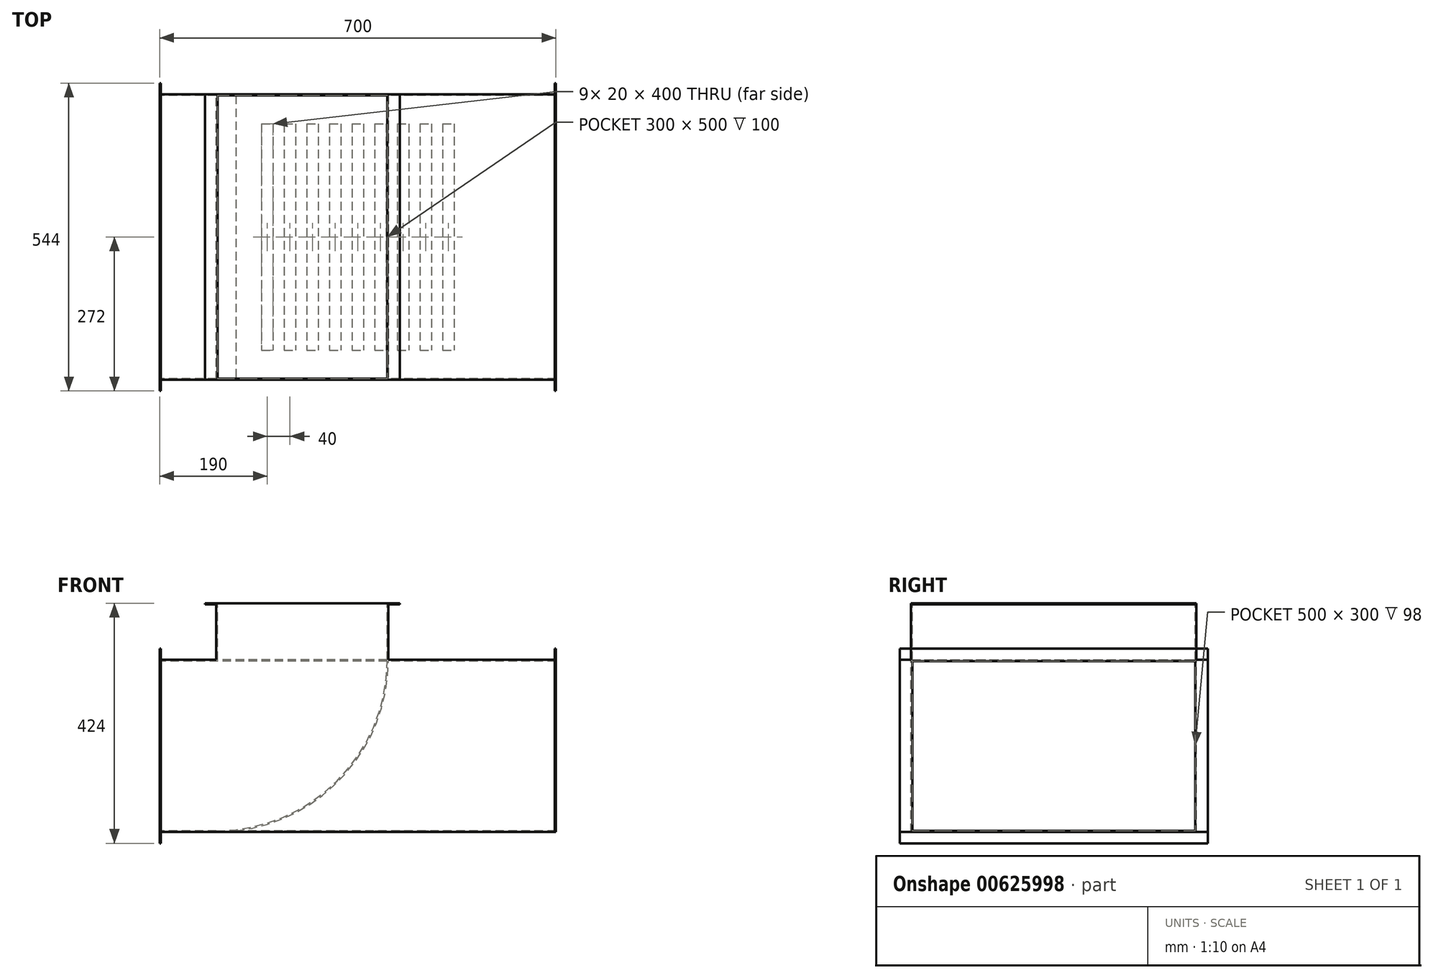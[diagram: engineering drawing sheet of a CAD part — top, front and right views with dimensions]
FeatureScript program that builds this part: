
annotation { "Feature Type Name" : "Feature", "Feature Type Description" : "" }
export const myFeature = defineFeature(function(context is Context, id is Id, definition is map)
    precondition{}
    {
        {
            var Q0;
            Q0=qCreatedBy(makeId("Right.planeOp"),FACE);
            var sketch = newSketch(context, id + "F0", { "sketchPlane" : qUnion([Q0])});
            skLineSegment(sketch, "E0.bottom", {"start": v(0, 0) * mm, "end": v(504, 0) * mm});
            skLineSegment(sketch, "E0.top", {"start": v(0, 304) * mm, "end": v(504, 304) * mm});
            skLineSegment(sketch, "E0.left", {"start": v(0, 0) * mm, "end": v(0, 304) * mm});
            skLineSegment(sketch, "E0.right", {"start": v(504, 0) * mm, "end": v(504, 304) * mm});
            skLineSegment(sketch, "E1.top", {"start": v(0, 324) * mm, "end": v(504, 324) * mm});
            skLineSegment(sketch, "E1.left", {"start": v(0, 304) * mm, "end": v(0, 324) * mm});
            skLineSegment(sketch, "E1.right", {"start": v(504, 304) * mm, "end": v(504, 324) * mm});
            skLineSegment(sketch, "E2.bottom", {"start": v(0, 304) * mm, "end": v(-20, 304) * mm});
            skLineSegment(sketch, "E2.top", {"start": v(0, 0) * mm, "end": v(-20, 0) * mm});
            skLineSegment(sketch, "E2.left", {"start": v(0, 304) * mm, "end": v(0, 0) * mm});
            skLineSegment(sketch, "E2.right", {"start": v(-20, 304) * mm, "end": v(-20, 0) * mm});
            skLineSegment(sketch, "E3.bottom", {"start": v(504, 304) * mm, "end": v(524, 304) * mm});
            skLineSegment(sketch, "E3.top", {"start": v(504, 0) * mm, "end": v(524, 0) * mm});
            skLineSegment(sketch, "E3.left", {"start": v(504, 304) * mm, "end": v(504, 0) * mm});
            skLineSegment(sketch, "E3.right", {"start": v(524, 304) * mm, "end": v(524, 0) * mm});
            skLineSegment(sketch, "E4.bottom", {"start": v(504, 0) * mm, "end": v(0, 0) * mm});
            skLineSegment(sketch, "E4.top", {"start": v(504, -20) * mm, "end": v(0, -20) * mm});
            skLineSegment(sketch, "E4.left", {"start": v(504, 0) * mm, "end": v(504, -20) * mm});
            skLineSegment(sketch, "E4.right", {"start": v(0, 0) * mm, "end": v(0, -20) * mm});
            skLineSegment(sketch, "E5.bottom", {"start": v(2, 2) * mm, "end": v(502, 2) * mm});
            skLineSegment(sketch, "E5.top", {"start": v(2, 302) * mm, "end": v(502, 302) * mm});
            skLineSegment(sketch, "E5.left", {"start": v(2, 2) * mm, "end": v(2, 302) * mm});
            skLineSegment(sketch, "E5.right", {"start": v(502, 2) * mm, "end": v(502, 302) * mm});
            skSolve(sketch);
        }
        {
            var Q0;
            Q0=makeQuery(id+"F0.imprint","IMPRINT",FACE,{"disambiguationData":[TD([[makeQuery(id+"F0.imprint","IMPRINT",EDGE,{"derivedFrom":sQuery(id+"F0.wireOp",EDGE,"E0.top")}),-1.0]])]});
            extrude(context, id + "F1", {"entities" : qUnion([Q0]), "depth" : 700 * mm, "offsetDistance" : 25 * mm});
        }
        {
            var Q0;
            Q0=makeQuery(id+"F0.imprint","IMPRINT",FACE,{"disambiguationData":[TD([[makeQuery(id+"F0.imprint","IMPRINT",EDGE,{"derivedFrom":sQuery(id+"F0.wireOp",EDGE,"E0.top")}),1.0]])]});
            var Q1;
            Q1=makeQuery(id+"F0.imprint","IMPRINT",FACE,{"disambiguationData":[TD([[makeQuery(id+"F0.imprint","IMPRINT",EDGE,{"derivedFrom":sQuery(id+"F0.wireOp",EDGE,"E2.bottom")}),1.0]])]});
            var Q2;
            Q2=makeQuery(id+"F0.imprint","IMPRINT",FACE,{"disambiguationData":[TD([[makeQuery(id+"F0.imprint","IMPRINT",EDGE,{"derivedFrom":sQuery(id+"F0.wireOp",EDGE,"E4.bottom")}),1.0]])]});
            var Q3;
            Q3=makeQuery(id+"F0.imprint","IMPRINT",FACE,{"disambiguationData":[TD([[makeQuery(id+"F0.imprint","IMPRINT",EDGE,{"derivedFrom":sQuery(id+"F0.wireOp",EDGE,"E3.bottom")}),-1.0]])]});
            extrude(context, id + "F2", {"entities" : qUnion([Q0, Q1, Q2, Q3]), "operationType" : NewBodyOperationType.ADD, "depth" : 700 * mm, "offsetDistance" : 25 * mm});
        }
        {
            var Q0;
            Q0=makeQuery(id+"F0.imprint","IMPRINT",FACE,{"disambiguationData":[TD([[makeQuery(id+"F0.imprint","IMPRINT",EDGE,{"derivedFrom":sQuery(id+"F0.wireOp",EDGE,"E0.top")}),1.0]])]});
            var Q1;
            Q1=makeQuery(id+"F0.imprint","IMPRINT",FACE,{"disambiguationData":[TD([[makeQuery(id+"F0.imprint","IMPRINT",EDGE,{"derivedFrom":sQuery(id+"F0.wireOp",EDGE,"E3.bottom")}),-1.0]])]});
            var Q2;
            Q2=makeQuery(id+"F0.imprint","IMPRINT",FACE,{"disambiguationData":[TD([[makeQuery(id+"F0.imprint","IMPRINT",EDGE,{"derivedFrom":sQuery(id+"F0.wireOp",EDGE,"E4.bottom")}),1.0]])]});
            var Q3;
            Q3=makeQuery(id+"F0.imprint","IMPRINT",FACE,{"disambiguationData":[TD([[makeQuery(id+"F0.imprint","IMPRINT",EDGE,{"derivedFrom":sQuery(id+"F0.wireOp",EDGE,"E2.bottom")}),1.0]])]});
            extrude(context, id + "F3", {"entities" : qUnion([Q0, Q1, Q2, Q3]), "operationType" : NewBodyOperationType.REMOVE, "depth" : 698 * mm, "offsetDistance" : 25 * mm});
        }
        {
            var Q0;
            Q0=makeQuery(id+"F0.imprint","IMPRINT",FACE,{"disambiguationData":[TD([[makeQuery(id+"F0.imprint","IMPRINT",EDGE,{"derivedFrom":sQuery(id+"F0.wireOp",EDGE,"E0.top")}),1.0]])]});
            var Q1;
            Q1=makeQuery(id+"F0.imprint","IMPRINT",FACE,{"disambiguationData":[TD([[makeQuery(id+"F0.imprint","IMPRINT",EDGE,{"derivedFrom":sQuery(id+"F0.wireOp",EDGE,"E3.bottom")}),-1.0]])]});
            var Q2;
            Q2=makeQuery(id+"F0.imprint","IMPRINT",FACE,{"disambiguationData":[TD([[makeQuery(id+"F0.imprint","IMPRINT",EDGE,{"derivedFrom":sQuery(id+"F0.wireOp",EDGE,"E4.bottom")}),1.0]])]});
            var Q3;
            Q3=makeQuery(id+"F0.imprint","IMPRINT",FACE,{"disambiguationData":[TD([[makeQuery(id+"F0.imprint","IMPRINT",EDGE,{"derivedFrom":sQuery(id+"F0.wireOp",EDGE,"E2.bottom")}),1.0]])]});
            extrude(context, id + "F4", {"entities" : qUnion([Q0, Q1, Q2, Q3]), "operationType" : NewBodyOperationType.ADD, "depth" : 2 * mm, "offsetDistance" : 25 * mm});
        }
        {
            var Q0;
            Q0=makeQuery(id+"F1.opExtrude","CAP_VERTEX",VERTEX,{"disambiguationData":[OSD([sQuery(id+"F0.wireOp",EDGE,"E5.top"),sQuery(id+"F0.wireOp",EDGE,"E5.left")])],"isStart":false});
            var Q1;
            Q1=makeQuery(id+"F1.opExtrude","CAP_VERTEX",VERTEX,{"disambiguationData":[OSD([sQuery(id+"F0.wireOp",EDGE,"E5.top"),sQuery(id+"F0.wireOp",EDGE,"E5.right")])],"isStart":false});
            var Q2;
            Q2=makeQuery(id+"F1.opExtrude","CAP_VERTEX",VERTEX,{"disambiguationData":[OSD([sQuery(id+"F0.wireOp",EDGE,"E5.bottom"),sQuery(id+"F0.wireOp",EDGE,"E5.right")])],"isStart":false});
            cPlane(context, id + "F5", {"entities" : qUnion([Q0, Q1, Q2]), "cplaneType" : CPlaneType.THREE_POINT, "offset" : 25 * mm, "width" : 150 * mm, "height" : 150 * mm});
        }
        {
            var Q0;
            Q0=qCreatedBy(id+"F5.planeOp",FACE);
            var sketch = newSketch(context, id + "F6", { "sketchPlane" : qUnion([Q0])});
            skLineSegment(sketch, "E6.0", {"start": v(2, 2) * mm, "end": v(2, 302) * mm});
            skLineSegment(sketch, "E7.0", {"start": v(2, 302) * mm, "end": v(502, 302) * mm});
            skLineSegment(sketch, "E8.0", {"start": v(502, 2) * mm, "end": v(502, 302) * mm});
            skLineSegment(sketch, "E9.0", {"start": v(2, 2) * mm, "end": v(502, 2) * mm});
            skSolve(sketch);
        }
        {
            var Q0;
            Q0=makeQuery(id+"F1.opExtrude","SWEPT_BODY",BODY,{"disambiguationData":[OSD([sQuery(id+"F0.wireOp",EDGE,"E0.top"),sQuery(id+"F0.wireOp",EDGE,"E2.left"),sQuery(id+"F0.wireOp",EDGE,"E3.left"),sQuery(id+"F0.wireOp",EDGE,"E4.bottom"),sQuery(id+"F0.wireOp",EDGE,"E5.bottom"),sQuery(id+"F0.wireOp",EDGE,"E5.top"),sQuery(id+"F0.wireOp",EDGE,"E5.left"),sQuery(id+"F0.wireOp",EDGE,"E5.right")])]});
            transform(context, id + "F7", {"entities" : qUnion([Q0]), "transformType" : TransformType.TRANSLATION_3D, "dx" : 0 * mm, "dy" : 0 * mm, "dz" : 0 * mm, "makeCopy" : true});
        }
        {
            var Q0;
            Q0=makeQuery(id+"F7.opPattern","COPY",FACE,{"derivedFrom":makeQuery(id+"F4.boolean.opBoolean","MERGE",FACE,{"disambiguationData":[OD(0.0)],"derivedFrom":[makeQuery(id+"F3.boolean.opBoolean","COPY",FACE,{"derivedFrom":makeQuery(id+"F3.opExtrude","SWEPT_FACE",FACE,{"disambiguationData":[OSD([sQuery(id+"F0.wireOp",EDGE,"E4.bottom")])]})}),makeQuery(id+"F4.opExtrude","SWEPT_FACE",FACE,{"disambiguationData":[OSD([sQuery(id+"F0.wireOp",EDGE,"E2.top")])]}),makeQuery(id+"F4.opExtrude","SWEPT_FACE",FACE,{"disambiguationData":[OSD([sQuery(id+"F0.wireOp",EDGE,"E3.top")])]})]}),"instanceName":"1"});
            var sketch = newSketch(context, id + "F8", { "sketchPlane" : qUnion([Q0])});
            skLineSegment(sketch, "E10.0.0", {"start": v(2, 0) * mm, "end": v(2, -504) * mm});
            skLineSegment(sketch, "E10.0.1", {"start": v(2, -504) * mm, "end": v(698, -504) * mm});
            skLineSegment(sketch, "E10.0.2", {"start": v(698, -504) * mm, "end": v(698, 0) * mm});
            skLineSegment(sketch, "E10.0.3", {"start": v(698, 0) * mm, "end": v(2, 0) * mm});
            skLineSegment(sketch, "E11.bottom", {"start": v(360, -52) * mm, "end": v(340, -52) * mm});
            skLineSegment(sketch, "E11.top", {"start": v(360, -452) * mm, "end": v(340, -452) * mm});
            skLineSegment(sketch, "E11.left", {"start": v(360, -52) * mm, "end": v(360, -452) * mm});
            skLineSegment(sketch, "E11.right", {"start": v(340, -52) * mm, "end": v(340, -452) * mm});
            skPoint(sketch, "E11.middle", {"position": v(350, -252) * mm});
            skPoint(sketch, "E11.middle.positionSnap0", {"position": v(2, -252) * mm});
            skPoint(sketch, "E11.middle.positionSnap1", {"position": v(350, -504) * mm});
            skPoint(sketch, "E11.centerSnap0", {"position": v(2, -252) * mm});
            skPoint(sketch, "E11.centerSnap1", {"position": v(350, -504) * mm});
            skLineSegment(sketch, "E12.1.0.0", {"start": v(380, -52) * mm, "end": v(380, -452) * mm});
            skLineSegment(sketch, "E12.1.0.1", {"start": v(400, -52) * mm, "end": v(400, -452) * mm});
            skPoint(sketch, "E12.1.0.2", {"position": v(390, -252) * mm});
            skLineSegment(sketch, "E12.1.0.3", {"start": v(400, -52) * mm, "end": v(380, -52) * mm});
            skLineSegment(sketch, "E12.1.0.4", {"start": v(400, -452) * mm, "end": v(380, -452) * mm});
            skLineSegment(sketch, "E12.2.0.0", {"start": v(420, -52) * mm, "end": v(420, -452) * mm});
            skLineSegment(sketch, "E12.2.0.1", {"start": v(440, -52) * mm, "end": v(440, -452) * mm});
            skPoint(sketch, "E12.2.0.2", {"position": v(430, -252) * mm});
            skLineSegment(sketch, "E12.2.0.3", {"start": v(440, -52) * mm, "end": v(420, -52) * mm});
            skLineSegment(sketch, "E12.2.0.4", {"start": v(440, -452) * mm, "end": v(420, -452) * mm});
            skLineSegment(sketch, "E12.3.0.0", {"start": v(460, -52) * mm, "end": v(460, -452) * mm});
            skLineSegment(sketch, "E12.3.0.1", {"start": v(480, -52) * mm, "end": v(480, -452) * mm});
            skPoint(sketch, "E12.3.0.2", {"position": v(470, -252) * mm});
            skLineSegment(sketch, "E12.3.0.3", {"start": v(480, -52) * mm, "end": v(460, -52) * mm});
            skLineSegment(sketch, "E12.3.0.4", {"start": v(480, -452) * mm, "end": v(460, -452) * mm});
            skLineSegment(sketch, "E12.4.0.0", {"start": v(500, -52) * mm, "end": v(500, -452) * mm});
            skLineSegment(sketch, "E12.4.0.1", {"start": v(520, -52) * mm, "end": v(520, -452) * mm});
            skPoint(sketch, "E12.4.0.2", {"position": v(510, -252) * mm});
            skLineSegment(sketch, "E12.4.0.3", {"start": v(520, -52) * mm, "end": v(500, -52) * mm});
            skLineSegment(sketch, "E12.4.0.4", {"start": v(520, -452) * mm, "end": v(500, -452) * mm});
            skLineSegment(sketch, "E12.direction1", {"start": v(340, -452) * mm, "end": v(380, -452) * mm, "construction": true});
            skLineSegment(sketch, "E13.1.0.0", {"start": v(320, -52) * mm, "end": v(320, -452) * mm});
            skLineSegment(sketch, "E13.1.0.1", {"start": v(300, -52) * mm, "end": v(300, -452) * mm});
            skPoint(sketch, "E13.1.0.2", {"position": v(310, -252) * mm});
            skLineSegment(sketch, "E13.1.0.3", {"start": v(320, -452) * mm, "end": v(300, -452) * mm});
            skLineSegment(sketch, "E13.1.0.4", {"start": v(320, -52) * mm, "end": v(300, -52) * mm});
            skLineSegment(sketch, "E13.2.0.0", {"start": v(280, -52) * mm, "end": v(280, -452) * mm});
            skLineSegment(sketch, "E13.2.0.1", {"start": v(260, -52) * mm, "end": v(260, -452) * mm});
            skPoint(sketch, "E13.2.0.2", {"position": v(270, -252) * mm});
            skLineSegment(sketch, "E13.2.0.3", {"start": v(280, -452) * mm, "end": v(260, -452) * mm});
            skLineSegment(sketch, "E13.2.0.4", {"start": v(280, -52) * mm, "end": v(260, -52) * mm});
            skLineSegment(sketch, "E13.3.0.0", {"start": v(240, -52) * mm, "end": v(240, -452) * mm});
            skLineSegment(sketch, "E13.3.0.1", {"start": v(220, -52) * mm, "end": v(220, -452) * mm});
            skPoint(sketch, "E13.3.0.2", {"position": v(230, -252) * mm});
            skLineSegment(sketch, "E13.3.0.3", {"start": v(240, -452) * mm, "end": v(220, -452) * mm});
            skLineSegment(sketch, "E13.3.0.4", {"start": v(240, -52) * mm, "end": v(220, -52) * mm});
            skLineSegment(sketch, "E13.4.0.0", {"start": v(200, -52) * mm, "end": v(200, -452) * mm});
            skLineSegment(sketch, "E13.4.0.1", {"start": v(180, -52) * mm, "end": v(180, -452) * mm});
            skPoint(sketch, "E13.4.0.2", {"position": v(190, -252) * mm});
            skLineSegment(sketch, "E13.4.0.3", {"start": v(200, -452) * mm, "end": v(180, -452) * mm});
            skLineSegment(sketch, "E13.4.0.4", {"start": v(200, -52) * mm, "end": v(180, -52) * mm});
            skLineSegment(sketch, "E13.direction1", {"start": v(340, -452) * mm, "end": v(300, -452) * mm, "construction": true});
            skSolve(sketch);
        }
        {
            var Q0;
            Q0=makeQuery(id+"F8.imprint","IMPRINT",FACE,{"disambiguationData":[TD([[makeQuery(id+"F8.imprint","IMPRINT",EDGE,{"derivedFrom":sQuery(id+"F8.wireOp",EDGE,"E13.4.0.0")}),-1.0]])]});
            var Q1;
            Q1=makeQuery(id+"F8.imprint","IMPRINT",FACE,{"disambiguationData":[TD([[makeQuery(id+"F8.imprint","IMPRINT",EDGE,{"derivedFrom":sQuery(id+"F8.wireOp",EDGE,"E13.3.0.0")}),-1.0]])]});
            var Q2;
            Q2=makeQuery(id+"F8.imprint","IMPRINT",FACE,{"disambiguationData":[TD([[makeQuery(id+"F8.imprint","IMPRINT",EDGE,{"derivedFrom":sQuery(id+"F8.wireOp",EDGE,"E13.2.0.0")}),-1.0]])]});
            var Q3;
            Q3=makeQuery(id+"F8.imprint","IMPRINT",FACE,{"disambiguationData":[TD([[makeQuery(id+"F8.imprint","IMPRINT",EDGE,{"derivedFrom":sQuery(id+"F8.wireOp",EDGE,"E13.1.0.0")}),-1.0]])]});
            var Q4;
            Q4=makeQuery(id+"F8.imprint","IMPRINT",FACE,{"disambiguationData":[TD([[makeQuery(id+"F8.imprint","IMPRINT",EDGE,{"derivedFrom":sQuery(id+"F8.wireOp",EDGE,"E11.bottom")}),1.0]])]});
            var Q5;
            Q5=makeQuery(id+"F8.imprint","IMPRINT",FACE,{"disambiguationData":[TD([[makeQuery(id+"F8.imprint","IMPRINT",EDGE,{"derivedFrom":sQuery(id+"F8.wireOp",EDGE,"E12.1.0.0")}),1.0]])]});
            var Q6;
            Q6=makeQuery(id+"F8.imprint","IMPRINT",FACE,{"disambiguationData":[TD([[makeQuery(id+"F8.imprint","IMPRINT",EDGE,{"derivedFrom":sQuery(id+"F8.wireOp",EDGE,"E12.2.0.0")}),1.0]])]});
            var Q7;
            Q7=makeQuery(id+"F8.imprint","IMPRINT",FACE,{"disambiguationData":[TD([[makeQuery(id+"F8.imprint","IMPRINT",EDGE,{"derivedFrom":sQuery(id+"F8.wireOp",EDGE,"E12.3.0.0")}),1.0]])]});
            var Q8;
            Q8=makeQuery(id+"F8.imprint","IMPRINT",FACE,{"disambiguationData":[TD([[makeQuery(id+"F8.imprint","IMPRINT",EDGE,{"derivedFrom":sQuery(id+"F8.wireOp",EDGE,"E12.4.0.0")}),1.0]])]});
            extrude(context, id + "F9", {"entities" : qUnion([Q0, Q1, Q2, Q3, Q4, Q5, Q6, Q7, Q8]), "operationType" : NewBodyOperationType.REMOVE, "oppositeDirection" : true, "depth" : 25 * mm, "offsetDistance" : 25 * mm});
        }
        {
            var Q0;
            {var subQ0=sQuery(id+"F0.wireOp",EDGE,"E4.right");var subQ1=sQuery(id+"F0.wireOp",EDGE,"E4.left");var subQ2=sQuery(id+"F0.wireOp",EDGE,"E4.top");var subQ3=sQuery(id+"F0.wireOp",EDGE,"E4.bottom");var subQ4=sQuery(id+"F0.wireOp",EDGE,"E3.right");var subQ5=sQuery(id+"F0.wireOp",EDGE,"E3.left");var subQ6=sQuery(id+"F0.wireOp",EDGE,"E3.top");var subQ7=sQuery(id+"F0.wireOp",EDGE,"E3.bottom");var subQ8=sQuery(id+"F0.wireOp",EDGE,"E2.right");var subQ9=sQuery(id+"F0.wireOp",EDGE,"E2.left");var subQ10=sQuery(id+"F0.wireOp",EDGE,"E2.top");var subQ11=sQuery(id+"F0.wireOp",EDGE,"E2.bottom");var subQ12=sQuery(id+"F0.wireOp",EDGE,"E1.right");var subQ13=sQuery(id+"F0.wireOp",EDGE,"E1.left");var subQ14=sQuery(id+"F0.wireOp",EDGE,"E1.top");var subQ15=sQuery(id+"F0.wireOp",EDGE,"E0.top");Q0=makeQuery(id+"F7.opPattern","COPY",FACE,{"derivedFrom":makeQuery(id+"F4.boolean.opBoolean","MERGE",FACE,{"derivedFrom":[makeQuery(id+"F2.boolean.opBoolean","MERGE",FACE,{"derivedFrom":[makeQuery(id+"F1.opExtrude","CAP_FACE",FACE,{"disambiguationData":[OSD([subQ15,subQ9,subQ5,subQ3,sQuery(id+"F0.wireOp",EDGE,"E5.bottom"),sQuery(id+"F0.wireOp",EDGE,"E5.top"),sQuery(id+"F0.wireOp",EDGE,"E5.left"),sQuery(id+"F0.wireOp",EDGE,"E5.right")])],"isStart":true}),makeQuery(id+"F2.opExtrude","CAP_FACE",FACE,{"disambiguationData":[OSD([subQ15,subQ14,subQ13,subQ12])],"isStart":true}),makeQuery(id+"F2.opExtrude","CAP_FACE",FACE,{"disambiguationData":[OSD([subQ11,subQ10,subQ9,subQ8])],"isStart":true}),makeQuery(id+"F2.opExtrude","CAP_FACE",FACE,{"disambiguationData":[OSD([subQ7,subQ6,subQ5,subQ4])],"isStart":true}),makeQuery(id+"F2.opExtrude","CAP_FACE",FACE,{"disambiguationData":[OSD([subQ3,subQ2,subQ1,subQ0])],"isStart":true})]}),makeQuery(id+"F4.opExtrude","CAP_FACE",FACE,{"disambiguationData":[OSD([subQ15,subQ14,subQ13,subQ12])],"isStart":true}),makeQuery(id+"F4.opExtrude","CAP_FACE",FACE,{"disambiguationData":[OSD([subQ11,subQ10,subQ9,subQ8])],"isStart":true}),makeQuery(id+"F4.opExtrude","CAP_FACE",FACE,{"disambiguationData":[OSD([subQ7,subQ6,subQ5,subQ4])],"isStart":true}),makeQuery(id+"F4.opExtrude","CAP_FACE",FACE,{"disambiguationData":[OSD([subQ3,subQ2,subQ1,subQ0])],"isStart":true})]}),"instanceName":"1"});}
            var sketch = newSketch(context, id + "F10", { "sketchPlane" : qUnion([Q0])});
            skPoint(sketch, "E14", {"position": v(-252, 152) * mm});
            skPoint(sketch, "E14.positionSnap0", {"position": v(-502, 152) * mm});
            skPoint(sketch, "E14.positionSnap1", {"position": v(-252, 302) * mm});
            skSolve(sketch);
        }
        {
            var Q0;
            {var subQ0=sQuery(id+"F0.wireOp",EDGE,"E4.bottom");var subQ1=sQuery(id+"F0.wireOp",EDGE,"E3.left");var subQ2=sQuery(id+"F0.wireOp",EDGE,"E2.left");var subQ3=sQuery(id+"F0.wireOp",EDGE,"E0.top");Q0=makeQuery(id+"F7.opPattern","COPY",FACE,{"derivedFrom":makeQuery(id+"F2.boolean.opBoolean","MERGE",FACE,{"derivedFrom":[makeQuery(id+"F1.opExtrude","CAP_FACE",FACE,{"disambiguationData":[OSD([subQ3,subQ2,subQ1,subQ0,sQuery(id+"F0.wireOp",EDGE,"E5.bottom"),sQuery(id+"F0.wireOp",EDGE,"E5.top"),sQuery(id+"F0.wireOp",EDGE,"E5.left"),sQuery(id+"F0.wireOp",EDGE,"E5.right")])],"isStart":false}),makeQuery(id+"F2.opExtrude","CAP_FACE",FACE,{"disambiguationData":[OSD([subQ3,sQuery(id+"F0.wireOp",EDGE,"E1.top"),sQuery(id+"F0.wireOp",EDGE,"E1.left"),sQuery(id+"F0.wireOp",EDGE,"E1.right")])],"isStart":false}),makeQuery(id+"F2.opExtrude","CAP_FACE",FACE,{"disambiguationData":[OSD([sQuery(id+"F0.wireOp",EDGE,"E2.bottom"),sQuery(id+"F0.wireOp",EDGE,"E2.top"),subQ2,sQuery(id+"F0.wireOp",EDGE,"E2.right")])],"isStart":false}),makeQuery(id+"F2.opExtrude","CAP_FACE",FACE,{"disambiguationData":[OSD([sQuery(id+"F0.wireOp",EDGE,"E3.bottom"),sQuery(id+"F0.wireOp",EDGE,"E3.top"),subQ1,sQuery(id+"F0.wireOp",EDGE,"E3.right")])],"isStart":false}),makeQuery(id+"F2.opExtrude","CAP_FACE",FACE,{"disambiguationData":[OSD([subQ0,sQuery(id+"F0.wireOp",EDGE,"E4.top"),sQuery(id+"F0.wireOp",EDGE,"E4.left"),sQuery(id+"F0.wireOp",EDGE,"E4.right")])],"isStart":false})]}),"instanceName":"1"});}
            var sketch = newSketch(context, id + "F11", { "sketchPlane" : qUnion([Q0])});
            skPoint(sketch, "E15", {"position": v(252, 152) * mm});
            skPoint(sketch, "E15.positionSnap0", {"position": v(2, 152) * mm});
            skPoint(sketch, "E15.positionSnap1", {"position": v(252, 302) * mm});
            skSolve(sketch);
        }
        {
            var Q0;
            Q0=qCreatedBy(makeId("Right.planeOp"),FACE);
            var sketch = newSketch(context, id + "F12", { "sketchPlane" : qUnion([Q0])});
            skPoint(sketch, "E16.0", {"position": v(504, 324) * mm});
            skPoint(sketch, "E17.0", {"position": v(-20, 304) * mm});
            skPoint(sketch, "E18.0", {"position": v(0, -20) * mm});
            skPoint(sketch, "E19.0", {"position": v(524, 0) * mm});
            skLineSegment(sketch, "E20.bottom", {"start": v(524, 324) * mm, "end": v(-20, 324) * mm});
            skLineSegment(sketch, "E20.top", {"start": v(524, -20) * mm, "end": v(-20, -20) * mm});
            skLineSegment(sketch, "E20.left", {"start": v(524, 324) * mm, "end": v(524, -20) * mm});
            skLineSegment(sketch, "E20.right", {"start": v(-20, 324) * mm, "end": v(-20, -20) * mm});
            skSolve(sketch);
        }
        {
            var Q0;
            Q0=makeQuery(id+"F12.imprint","IMPRINT",FACE,{"disambiguationData":[TD([[makeQuery(id+"F12.imprint","IMPRINT",EDGE,{"derivedFrom":sQuery(id+"F12.wireOp",EDGE,"E20.bottom")}),1.0]])]});
            extrude(context, id + "F13", {"entities" : qUnion([Q0]), "depth" : 2 * mm, "offsetDistance" : 25 * mm});
        }
        {
            var Q0;
            Q0=qCreatedBy(makeId("Front.planeOp"),FACE);
            var sketch = newSketch(context, id + "F14", { "sketchPlane" : qUnion([Q0])});
            skPoint(sketch, "E21.0", {"position": v(0, 304) * mm});
            skLineSegment(sketch, "E22", {"start": v(0, 0) * mm, "end": v(100, 0) * mm});
            skLineSegment(sketch, "E23", {"start": v(0, 304) * mm, "end": v(100, 304) * mm, "construction": true});
            skArc(sketch, "E24", {"start": v(100, 0) * mm, "mid": v(314.96, 89.04) * mm, "end": v(404, 304) * mm});
            skLineSegment(sketch, "E25", {"start": v(404, 304) * mm, "end": v(404, 404) * mm});
            skSolve(sketch);
        }
        {
            var Q0;
            Q0=makeQuery(id+"F0.imprint","IMPRINT",FACE,{"disambiguationData":[TD([[makeQuery(id+"F0.imprint","IMPRINT",EDGE,{"derivedFrom":sQuery(id+"F0.wireOp",EDGE,"E0.top")}),-1.0]])]});
            var Q1;
            Q1=qConstructionFilter(qBodyType(qCreatedBy(id+"F14",EDGE),BodyType.WIRE),ConstructionObject.NO);
            sweep(context, id + "F15", {"profiles" : qUnion([Q0]), "path" : qUnion([Q1])});
        }
        {
            var Q0;
            Q0=makeQuery(id+"F0.imprint","IMPRINT",FACE,{"disambiguationData":[TD([[makeQuery(id+"F0.imprint","IMPRINT",EDGE,{"derivedFrom":sQuery(id+"F0.wireOp",EDGE,"E0.top")}),1.0]])]});
            var Q1;
            Q1=makeQuery(id+"F0.imprint","IMPRINT",FACE,{"disambiguationData":[TD([[makeQuery(id+"F0.imprint","IMPRINT",EDGE,{"derivedFrom":sQuery(id+"F0.wireOp",EDGE,"E3.bottom")}),-1.0]])]});
            var Q2;
            Q2=makeQuery(id+"F0.imprint","IMPRINT",FACE,{"disambiguationData":[TD([[makeQuery(id+"F0.imprint","IMPRINT",EDGE,{"derivedFrom":sQuery(id+"F0.wireOp",EDGE,"E4.bottom")}),1.0]])]});
            var Q3;
            Q3=makeQuery(id+"F0.imprint","IMPRINT",FACE,{"disambiguationData":[TD([[makeQuery(id+"F0.imprint","IMPRINT",EDGE,{"derivedFrom":sQuery(id+"F0.wireOp",EDGE,"E2.bottom")}),1.0]])]});
            extrude(context, id + "F16", {"entities" : qUnion([Q0, Q1, Q2, Q3]), "operationType" : NewBodyOperationType.ADD, "depth" : 2 * mm, "offsetDistance" : 25 * mm});
        }
        {
            var Q0;
            Q0=makeQuery(id+"F15.opSweep","CAP_FACE",FACE,{"disambiguationData":[OSD([sQuery(id+"F0.wireOp",EDGE,"E0.top"),sQuery(id+"F0.wireOp",EDGE,"E2.left"),sQuery(id+"F0.wireOp",EDGE,"E3.left"),sQuery(id+"F0.wireOp",EDGE,"E4.bottom"),sQuery(id+"F0.wireOp",EDGE,"E5.bottom"),sQuery(id+"F0.wireOp",EDGE,"E5.top"),sQuery(id+"F0.wireOp",EDGE,"E5.left"),sQuery(id+"F0.wireOp",EDGE,"E5.right"),sQuery(id+"F14.wireOp",VERTEX,"E25.end")])],"isStart":false});
            var sketch = newSketch(context, id + "F17", { "sketchPlane" : qUnion([Q0])});
            skLineSegment(sketch, "E26.0", {"start": v(100, 0) * mm, "end": v(100, 504) * mm});
            skLineSegment(sketch, "E27.0", {"start": v(100, 0) * mm, "end": v(404, 0) * mm});
            skLineSegment(sketch, "E28.0", {"start": v(404, 504) * mm, "end": v(404, 0) * mm});
            skLineSegment(sketch, "E29.0", {"start": v(100, 504) * mm, "end": v(404, 504) * mm});
            skLineSegment(sketch, "E30.bottom", {"start": v(100, 504) * mm, "end": v(80, 504) * mm});
            skLineSegment(sketch, "E30.top", {"start": v(100, 0) * mm, "end": v(80, 0) * mm});
            skLineSegment(sketch, "E30.right", {"start": v(80, 504) * mm, "end": v(80, 0) * mm});
            skLineSegment(sketch, "E31.top", {"start": v(100, 524) * mm, "end": v(404, 524) * mm});
            skLineSegment(sketch, "E31.left", {"start": v(100, 504) * mm, "end": v(100, 524) * mm});
            skLineSegment(sketch, "E31.right", {"start": v(404, 504) * mm, "end": v(404, 524) * mm});
            skLineSegment(sketch, "E32.bottom", {"start": v(404, 504) * mm, "end": v(424, 504) * mm});
            skLineSegment(sketch, "E32.top", {"start": v(404, 0) * mm, "end": v(424, 0) * mm});
            skLineSegment(sketch, "E32.right", {"start": v(424, 504) * mm, "end": v(424, 0) * mm});
            skLineSegment(sketch, "E33.top", {"start": v(100, -20) * mm, "end": v(404, -20) * mm});
            skLineSegment(sketch, "E33.left", {"start": v(100, 0) * mm, "end": v(100, -20) * mm});
            skLineSegment(sketch, "E33.right", {"start": v(404, 0) * mm, "end": v(404, -20) * mm});
            skPoint(sketch, "E34", {"position": v(252, 252) * mm});
            skPoint(sketch, "E34.positionSnap0", {"position": v(252, 2) * mm});
            skPoint(sketch, "E34.positionSnap1", {"position": v(100, 252) * mm});
            skSolve(sketch);
        }
        {
            var Q0;
            Q0=makeQuery(id+"F17.imprint","IMPRINT",FACE,{"disambiguationData":[TD([[makeQuery(id+"F17.imprint","IMPRINT",EDGE,{"derivedFrom":sQuery(id+"F17.wireOp",EDGE,"E29.0")}),1.0]])]});
            var Q1;
            Q1=makeQuery(id+"F17.imprint","IMPRINT",FACE,{"disambiguationData":[TD([[makeQuery(id+"F17.imprint","IMPRINT",EDGE,{"derivedFrom":sQuery(id+"F17.wireOp",EDGE,"E26.0")}),1.0]])]});
            var Q2;
            Q2=makeQuery(id+"F17.imprint","IMPRINT",FACE,{"disambiguationData":[TD([[makeQuery(id+"F17.imprint","IMPRINT",EDGE,{"derivedFrom":sQuery(id+"F17.wireOp",EDGE,"E32.bottom")}),-1.0]])]});
            var Q3;
            Q3=makeQuery(id+"F17.imprint","IMPRINT",FACE,{"disambiguationData":[TD([[makeQuery(id+"F17.imprint","IMPRINT",EDGE,{"derivedFrom":sQuery(id+"F17.wireOp",EDGE,"E27.0")}),-1.0]])]});
            extrude(context, id + "F18", {"entities" : qUnion([Q0, Q1, Q2, Q3]), "operationType" : NewBodyOperationType.ADD, "oppositeDirection" : true, "depth" : 2 * mm, "offsetDistance" : 25 * mm});
        }
    });
